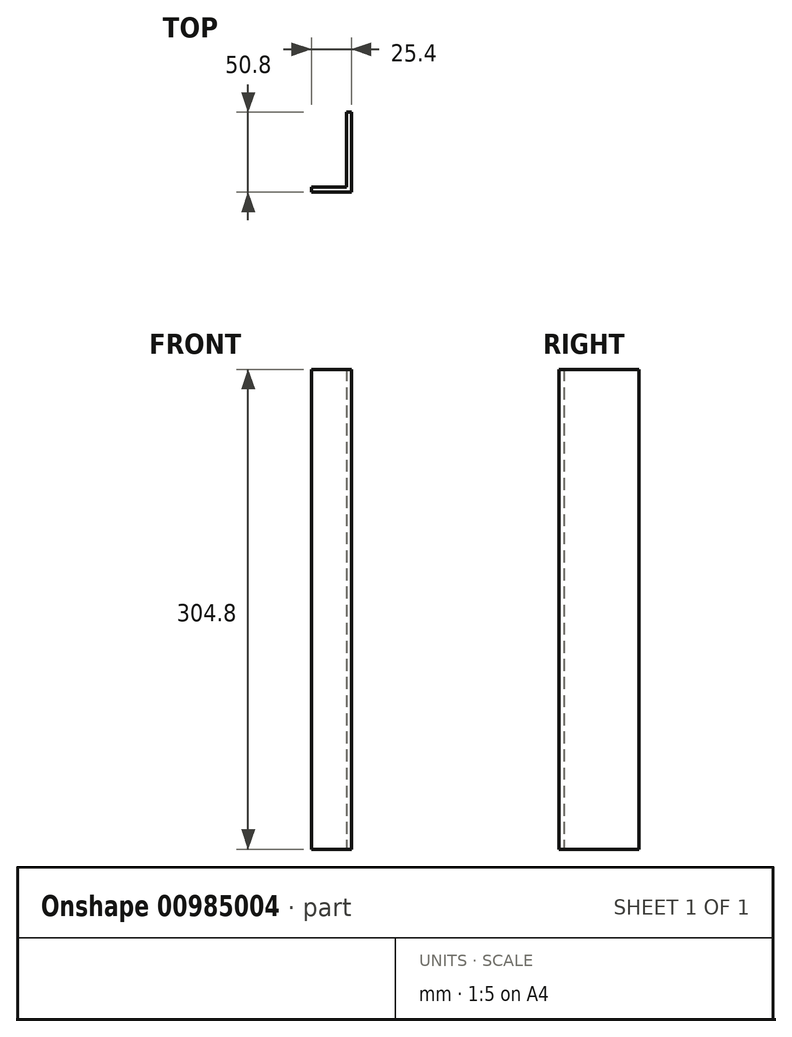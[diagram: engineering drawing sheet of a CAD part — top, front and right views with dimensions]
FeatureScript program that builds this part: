
annotation { "Feature Type Name" : "Feature", "Feature Type Description" : "" }
export const myFeature = defineFeature(function(context is Context, id is Id, definition is map)
    precondition{}
    {
        {
            var Q0;
            Q0=qCreatedBy(makeId("Top.planeOp"),FACE);
            var sketch = newSketch(context, id + "F0", { "sketchPlane" : qUnion([Q0])});
            skLineSegment(sketch, "E0.bottom", {"start": v(-3.18, 50.8) * mm, "end": v(0, 50.8) * mm});
            skLineSegment(sketch, "E0.left", {"start": v(-3.18, 50.8) * mm, "end": v(-3.18, 3.18) * mm});
            skLineSegment(sketch, "E0.right", {"start": v(0, 50.8) * mm, "end": v(0, 0) * mm});
            skLineSegment(sketch, "E1.bottom", {"start": v(-25.4, 3.18) * mm, "end": v(-3.18, 3.18) * mm});
            skLineSegment(sketch, "E1.left", {"start": v(-25.4, 3.18) * mm, "end": v(-25.4, 0) * mm});
            skLineSegment(sketch, "E2", {"start": v(-25.4, 0) * mm, "end": v(0, 0) * mm});
            skSolve(sketch);
        }
        {
            var Q0;
            Q0=makeQuery(id+"F0.imprint","IMPRINT",FACE,{"disambiguationData":[TD([[makeQuery(id+"F0.imprint","IMPRINT",EDGE,{"derivedFrom":sQuery(id+"F0.wireOp",EDGE,"E0.bottom")}),-1.0]])]});
            extrude(context, id + "F1", {"entities" : qUnion([Q0]), "depth" : 152.4 * mm, "offsetDistance" : 25.4 * mm, "hasSecondDirection" : true, "secondDirectionOppositeDirection" : true, "secondDirectionDepth" : 152.4 * mm});
        }
    });
